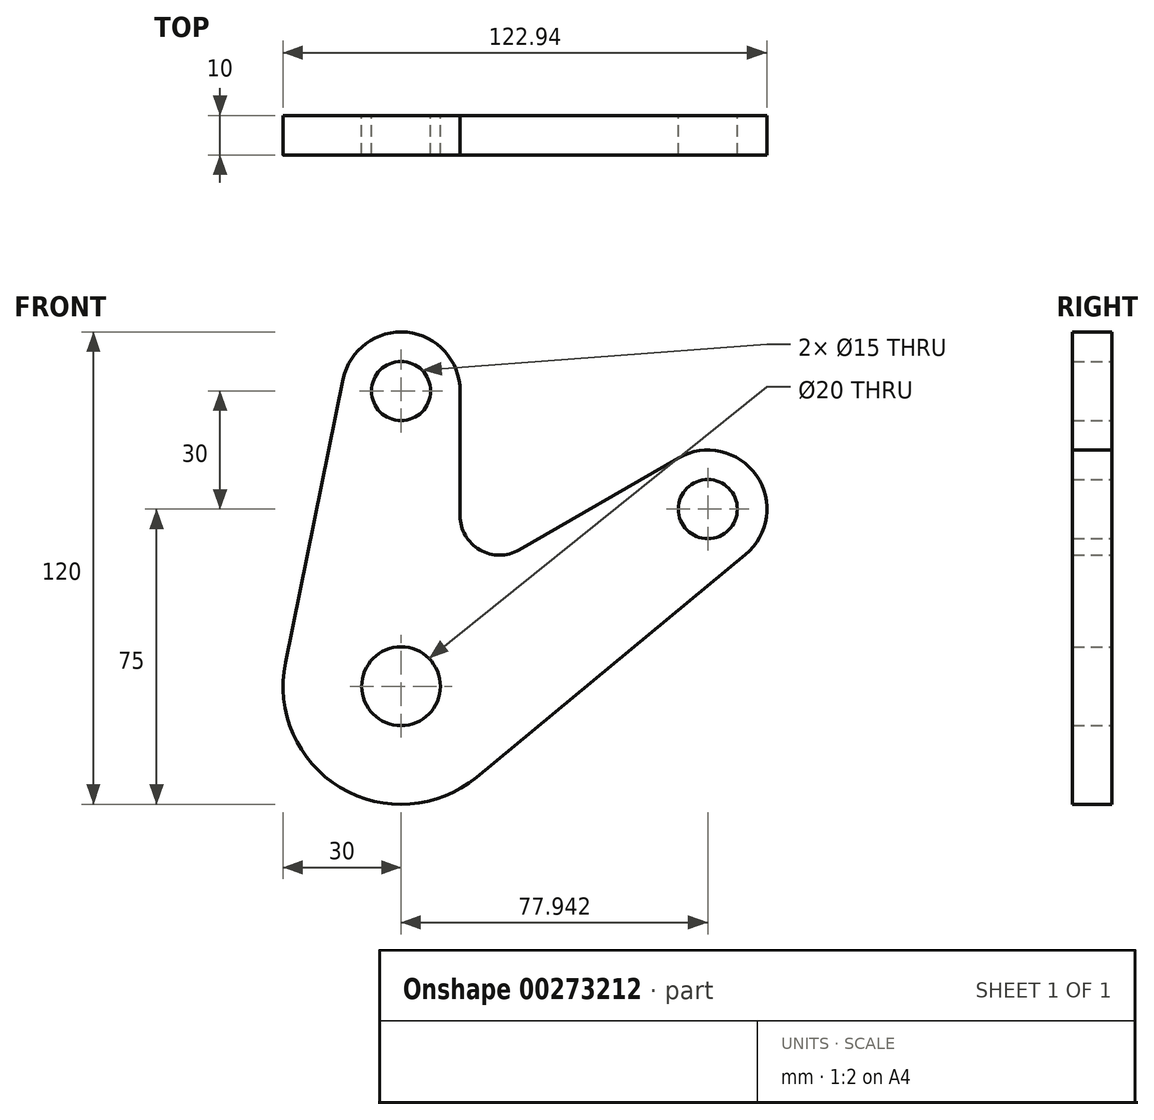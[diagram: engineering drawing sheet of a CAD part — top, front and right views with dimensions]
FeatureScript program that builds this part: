
annotation { "Feature Type Name" : "Feature", "Feature Type Description" : "" }
export const myFeature = defineFeature(function(context is Context, id is Id, definition is map)
    precondition{}
    {
        {
            var Q0;
            Q0=qCreatedBy(makeId("Front.planeOp"),FACE);
            var sketch = newSketch(context, id + "F0", { "sketchPlane" : qUnion([Q0])});
            skCircle(sketch, "E0", {"center": v(0, 0) * mm, "radius": 10 * mm});
            skCircle(sketch, "E1", {"center": v(77.94, 45) * mm, "radius": 7.5 * mm});
            skCircle(sketch, "E2", {"center": v(0, 75) * mm, "radius": 7.5 * mm});
            skLineSegment(sketch, "E3", {"start": v(15, 75) * mm, "end": v(15, 43.3) * mm});
            skLineSegment(sketch, "E4", {"start": v(0, 75) * mm, "end": v(0, 0) * mm, "construction": true});
            skLineSegment(sketch, "E5", {"start": v(77.94, 45) * mm, "end": v(0, 0) * mm, "construction": true});
            skLineSegment(sketch, "E6", {"start": v(30, 34.64) * mm, "end": v(70.44, 58) * mm});
            skArc(sketch, "E7", {"start": v(15, 43.3) * mm, "mid": v(20, 34.64) * mm, "end": v(30, 34.64) * mm});
            skLineSegment(sketch, "E8", {"start": v(-14.7, 78) * mm, "end": v(-29.4, 6) * mm});
            skArc(sketch, "E9", {"start": v(15, 75) * mm, "mid": v(1.5, 89.92) * mm, "end": v(-14.7, 78) * mm});
            skLineSegment(sketch, "E10", {"start": v(87.5, 33.44) * mm, "end": v(19.12, -23.12) * mm});
            skArc(sketch, "E11", {"start": v(87.5, 33.44) * mm, "mid": v(90.26, 53.56) * mm, "end": v(70.44, 58) * mm});
            skArc(sketch, "E12", {"start": v(-29.4, 6) * mm, "mid": v(-15.44, -25.72) * mm, "end": v(19.12, -23.12) * mm});
            skSolve(sketch);
        }
        {
            var Q0;
            Q0 = qSketchRegion(id + "F0", true);
            extrude(context, id + "F1", {"entities" : qUnion([Q0]), "depth" : 10 * mm});
        }
    });
